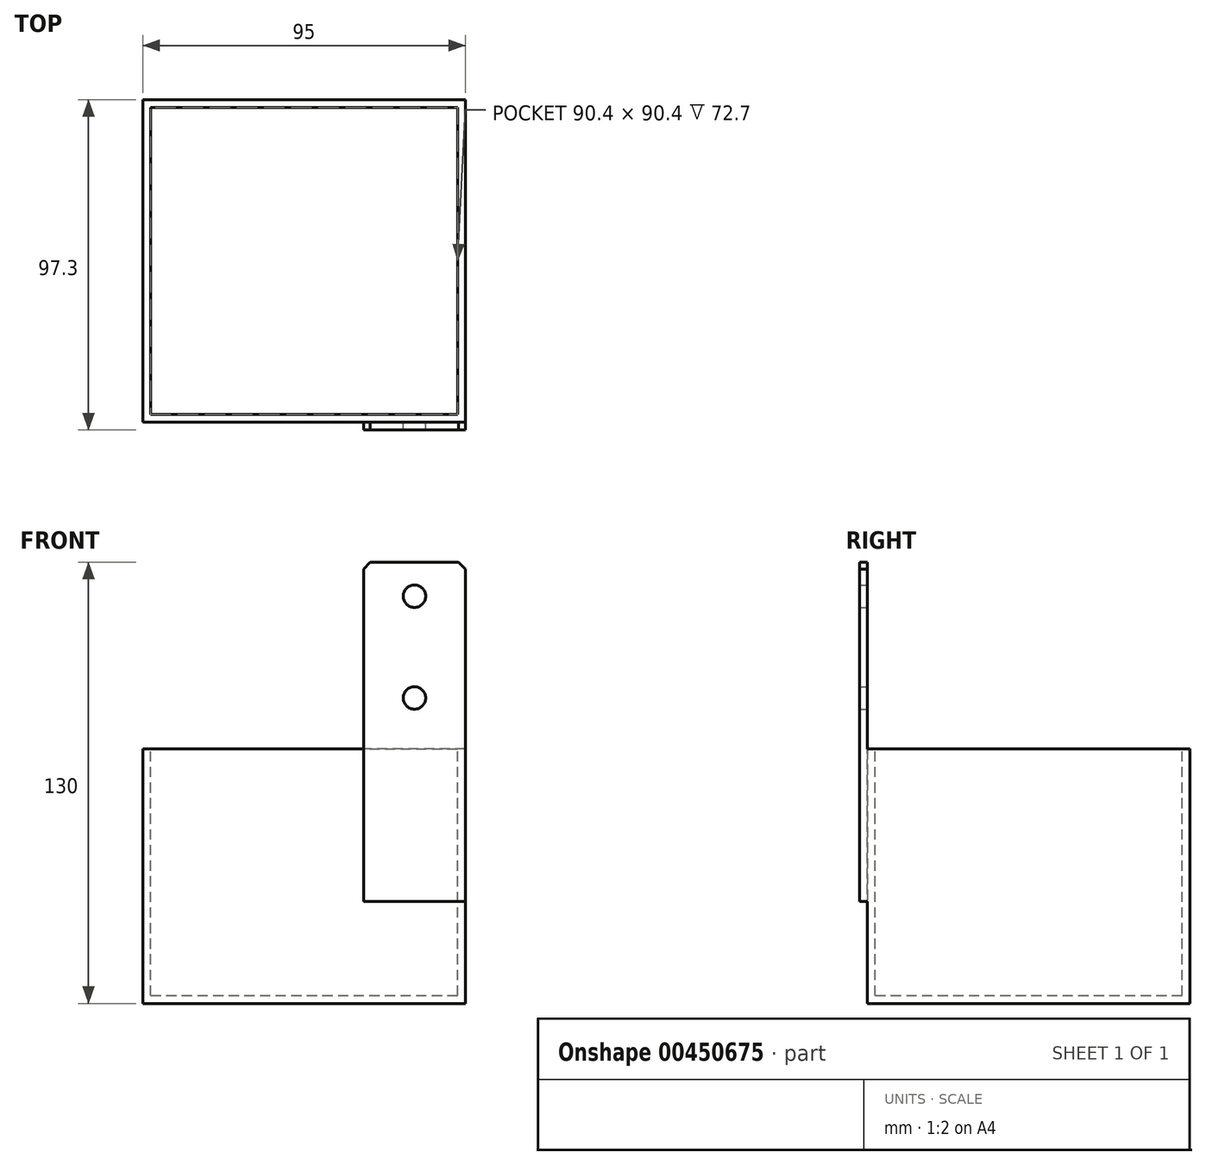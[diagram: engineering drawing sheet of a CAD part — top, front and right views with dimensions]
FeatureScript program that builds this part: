
annotation { "Feature Type Name" : "Feature", "Feature Type Description" : "" }
export const myFeature = defineFeature(function(context is Context, id is Id, definition is map)
    precondition{}
    {
        {
            var Q0;
            Q0=qCreatedBy(makeId("Front.planeOp"),FACE);
            var sketch = newSketch(context, id + "F0", { "sketchPlane" : qUnion([Q0])});
            skLineSegment(sketch, "E0", {"start": v(103.22, -62.28) * mm, "end": v(103.22, 10.42) * mm});
            skLineSegment(sketch, "E1", {"start": v(12.82, -62.28) * mm, "end": v(12.82, 10.42) * mm});
            skLineSegment(sketch, "E2", {"start": v(10.52, -64.58) * mm, "end": v(10.52, 10.42) * mm});
            skLineSegment(sketch, "E3", {"start": v(10.52, 65.42) * mm, "end": v(8.22, 65.42) * mm});
            skLineSegment(sketch, "E4", {"start": v(105.52, -64.58) * mm, "end": v(10.52, -64.58) * mm});
            skLineSegment(sketch, "E5", {"start": v(105.52, -64.58) * mm, "end": v(105.52, 10.42) * mm});
            skLineSegment(sketch, "E6", {"start": v(103.22, -62.28) * mm, "end": v(12.82, -62.28) * mm});
            skLineSegment(sketch, "E7", {"start": v(10.52, 10.42) * mm, "end": v(10.52, 65.42) * mm});
            skLineSegment(sketch, "E8", {"start": v(105.52, 10.42) * mm, "end": v(10.52, 10.42) * mm});
            skLineSegment(sketch, "E9", {"start": v(-74.22, -64.58) * mm, "end": v(-169.22, -64.58) * mm});
            skLineSegment(sketch, "E10", {"start": v(-76.52, -62.28) * mm, "end": v(-166.92, -62.28) * mm});
            skLineSegment(sketch, "E11", {"start": v(-74.22, 10.42) * mm, "end": v(-104.22, 10.42) * mm});
            skLineSegment(sketch, "E12", {"start": v(-104.22, 10.42) * mm, "end": v(-169.22, 10.42) * mm});
            skLineSegment(sketch, "E13", {"start": v(-74.22, -64.58) * mm, "end": v(-74.22, 10.42) * mm});
            skLineSegment(sketch, "E14", {"start": v(-169.22, -64.58) * mm, "end": v(-169.22, 10.42) * mm});
            skLineSegment(sketch, "E15", {"start": v(-166.92, -62.28) * mm, "end": v(-166.92, 10.42) * mm});
            skLineSegment(sketch, "E16", {"start": v(-76.52, -62.28) * mm, "end": v(-76.52, 10.42) * mm});
            skLineSegment(sketch, "E17", {"start": v(-76.22, 65.42) * mm, "end": v(-102.22, 65.42) * mm});
            skLineSegment(sketch, "E18", {"start": v(-74.22, 63.42) * mm, "end": v(-76.22, 65.42) * mm});
            skLineSegment(sketch, "E19", {"start": v(-74.22, -34.58) * mm, "end": v(-104.22, -34.58) * mm});
            skLineSegment(sketch, "E20", {"start": v(-74.22, 63.42) * mm, "end": v(-74.22, 10.42) * mm});
            skLineSegment(sketch, "E21", {"start": v(-104.22, 63.42) * mm, "end": v(-104.22, -34.58) * mm});
            skLineSegment(sketch, "E22", {"start": v(-102.22, 65.42) * mm, "end": v(-104.22, 63.42) * mm});
            skLineSegment(sketch, "E23", {"start": v(10.52, -34.58) * mm, "end": v(8.22, -34.58) * mm});
            skLineSegment(sketch, "E24", {"start": v(8.22, 65.42) * mm, "end": v(8.22, -34.58) * mm});
            skLineSegment(sketch, "E25", {"start": v(-93.12, 55.42) * mm, "end": v(-85.32, 55.42) * mm});
            skLineSegment(sketch, "E26", {"start": v(-89.22, 51.52) * mm, "end": v(-89.22, 59.32) * mm});
            skLineSegment(sketch, "E27", {"start": v(-93.12, 25.42) * mm, "end": v(-85.32, 25.42) * mm});
            skLineSegment(sketch, "E28", {"start": v(-89.22, 21.52) * mm, "end": v(-89.22, 29.32) * mm});
            skCircle(sketch, "E29", {"center": v(-89.22, 55.42) * mm, "radius": 3.3 * mm});
            skCircle(sketch, "E30", {"center": v(-89.22, 25.42) * mm, "radius": 3.3 * mm});
            skSolve(sketch);
        }
        {
            var Q0;
            {var subQ1=sQuery(id+"F0.wireOp",EDGE,"E11");var subQ3=sQuery(id+"F0.wireOp",EDGE,"E16");var subQ4=makeQuery(id+"F0.imprint","INTERSECT",VERTEX,{"derivedFrom":[subQ1,subQ3]});Q0=makeQuery(id+"F0.imprint","IMPRINT",FACE,{"disambiguationData":[TD([[makeQuery(id+"F0.imprint","IMPRINT",EDGE,{"disambiguationData":[TD([[subQ4,1.0]])],"derivedFrom":subQ3}),1.0]])]});}
            var Q1;
            Q1=makeQuery(id+"F0.imprint","IMPRINT",FACE,{"disambiguationData":[TD([[makeQuery(id+"F0.imprint","IMPRINT",EDGE,{"derivedFrom":sQuery(id+"F0.wireOp",EDGE,"E17")}),1.0]])]});
            var Q2;
            {var subQ1=sQuery(id+"F0.wireOp",EDGE,"E11");var subQ3=sQuery(id+"F0.wireOp",EDGE,"E16");var subQ4=makeQuery(id+"F0.imprint","INTERSECT",VERTEX,{"derivedFrom":[subQ1,subQ3]});Q2=makeQuery(id+"F0.imprint","IMPRINT",FACE,{"disambiguationData":[TD([[makeQuery(id+"F0.imprint","IMPRINT",EDGE,{"disambiguationData":[TD([[subQ4,1.0]])],"derivedFrom":subQ3}),-1.0]])]});}
            extrude(context, id + "F1", {"entities" : qUnion([Q0, Q1, Q2]), "depth" : 2.3 * mm});
        }
        {
            var Q0;
            {var subQ1=sQuery(id+"F0.wireOp",EDGE,"E10");Q0=makeQuery(id+"F0.imprint","IMPRINT",FACE,{"disambiguationData":[TD([[makeQuery(id+"F0.imprint","IMPRINT",EDGE,{"derivedFrom":subQ1}),-1.0]])]});}
            var Q1;
            {var subQ1=sQuery(id+"F0.wireOp",EDGE,"E9");Q1=makeQuery(id+"F0.imprint","IMPRINT",FACE,{"disambiguationData":[TD([[makeQuery(id+"F0.imprint","IMPRINT",EDGE,{"derivedFrom":subQ1}),-1.0]])]});}
            var Q2;
            {var subQ1=sQuery(id+"F0.wireOp",EDGE,"E11");var subQ3=sQuery(id+"F0.wireOp",EDGE,"E16");var subQ4=makeQuery(id+"F0.imprint","INTERSECT",VERTEX,{"derivedFrom":[subQ1,subQ3]});Q2=makeQuery(id+"F0.imprint","IMPRINT",FACE,{"disambiguationData":[TD([[makeQuery(id+"F0.imprint","IMPRINT",EDGE,{"disambiguationData":[TD([[subQ4,1.0]])],"derivedFrom":subQ3}),1.0]])]});}
            var Q3;
            {var subQ1=sQuery(id+"F0.wireOp",EDGE,"E11");var subQ3=sQuery(id+"F0.wireOp",EDGE,"E16");var subQ4=makeQuery(id+"F0.imprint","INTERSECT",VERTEX,{"derivedFrom":[subQ1,subQ3]});Q3=makeQuery(id+"F0.imprint","IMPRINT",FACE,{"disambiguationData":[TD([[makeQuery(id+"F0.imprint","IMPRINT",EDGE,{"disambiguationData":[TD([[subQ4,1.0]])],"derivedFrom":subQ3}),-1.0]])]});}
            extrude(context, id + "F2", {"entities" : qUnion([Q0, Q1, Q2, Q3]), "operationType" : NewBodyOperationType.ADD, "oppositeDirection" : true, "depth" : 95 * mm});
        }
        {
            var Q0;
            Q0=makeQuery(id+"F2.opExtrude","SWEPT_FACE",FACE,{"disambiguationData":[OSD([sQuery(id+"F0.wireOp",EDGE,"E11"),sQuery(id+"F0.wireOp",EDGE,"E12")])]});
            var sketch = newSketch(context, id + "F3", { "sketchPlane" : qUnion([Q0])});
            skLineSegment(sketch, "E31.0", {"start": v(-76.52, 2.3) * mm, "end": v(-76.52, 92.7) * mm});
            skLineSegment(sketch, "E31.1", {"start": v(-104.22, 2.3) * mm, "end": v(-76.52, 2.3) * mm});
            skLineSegment(sketch, "E31.2", {"start": v(-76.52, 92.7) * mm, "end": v(-166.92, 92.7) * mm});
            skLineSegment(sketch, "E31.3", {"start": v(-166.92, 92.7) * mm, "end": v(-166.92, 2.3) * mm});
            skLineSegment(sketch, "E31.4", {"start": v(-166.92, 2.3) * mm, "end": v(-104.22, 2.3) * mm});
            skSolve(sketch);
        }
        {
            var Q0;
            Q0 = qSketchRegion(id + "F3", true);
            extrude(context, id + "F4", {"entities" : qUnion([Q0]), "operationType" : NewBodyOperationType.REMOVE, "oppositeDirection" : true, "depth" : 72.7 * mm});
        }
    });
